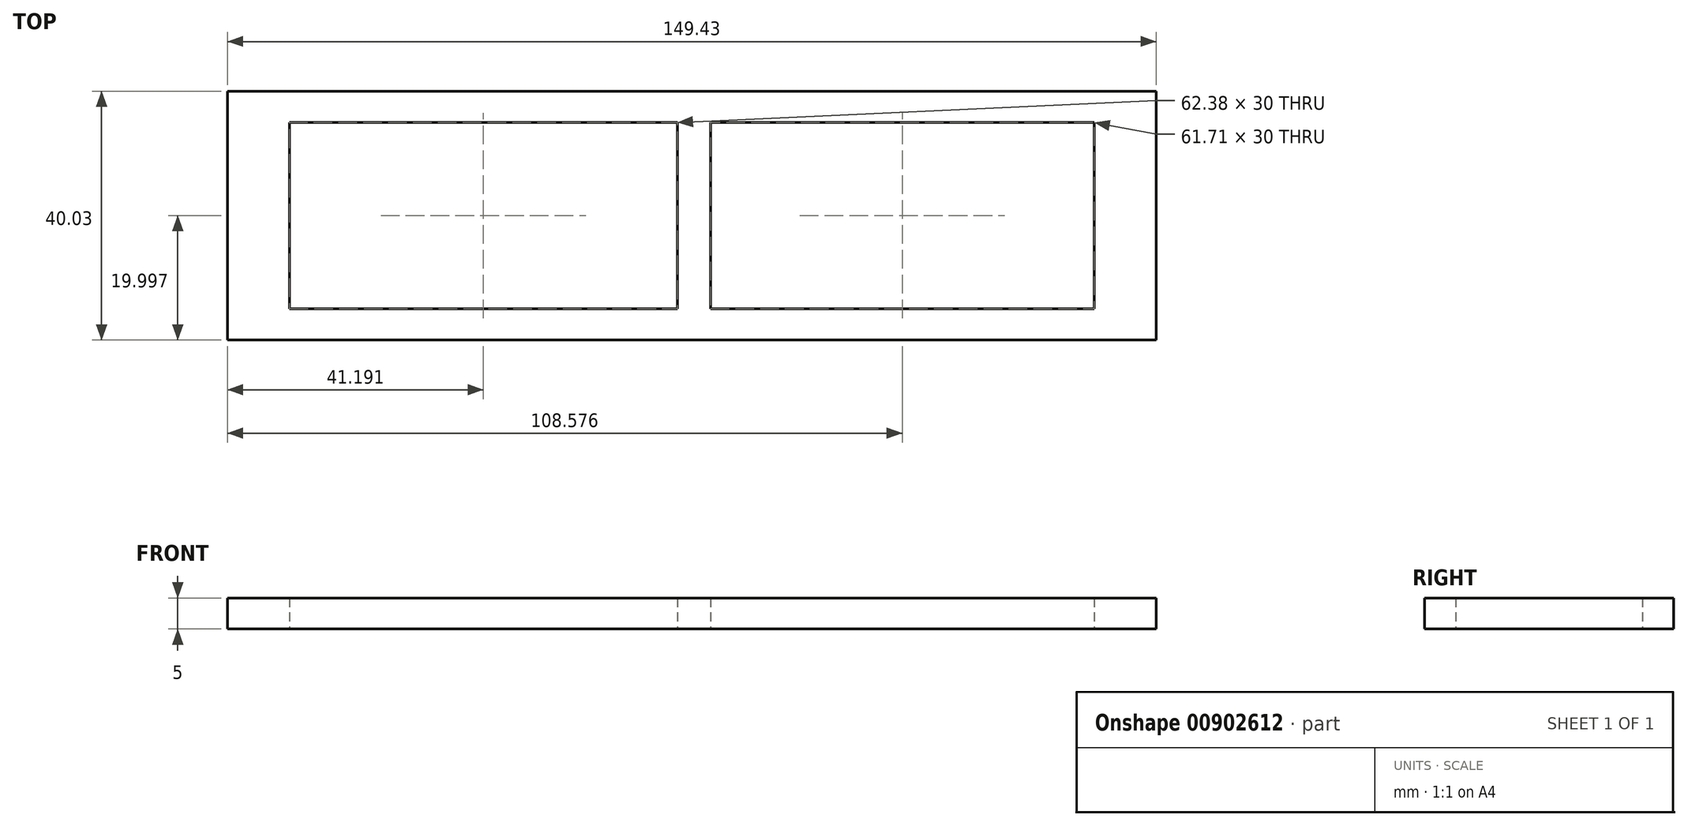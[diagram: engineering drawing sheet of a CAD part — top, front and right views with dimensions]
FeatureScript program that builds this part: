
annotation { "Feature Type Name" : "Feature", "Feature Type Description" : "" }
export const myFeature = defineFeature(function(context is Context, id is Id, definition is map)
    precondition{}
    {
        {
            var Q0;
            Q0=qCreatedBy(makeId("Top.planeOp"),FACE);
            var sketch = newSketch(context, id + "F0", { "sketchPlane" : qUnion([Q0])});
            skLineSegment(sketch, "E0.bottom", {"start": v(-75.17, 20.19) * mm, "end": v(-65.17, 20.19) * mm});
            skLineSegment(sketch, "E0.top", {"start": v(-75.17, -19.81) * mm, "end": v(-65.17, -19.81) * mm});
            skLineSegment(sketch, "E0.left", {"start": v(-75.17, 20.19) * mm, "end": v(-75.17, -19.81) * mm});
            skLineSegment(sketch, "E0.right", {"start": v(-65.17, 20.19) * mm, "end": v(-65.17, -19.81) * mm});
            skLineSegment(sketch, "E1.bottom", {"start": v(64.26, 20.22) * mm, "end": v(74.26, 20.22) * mm});
            skLineSegment(sketch, "E1.top", {"start": v(64.26, -19.78) * mm, "end": v(74.26, -19.78) * mm});
            skLineSegment(sketch, "E1.left", {"start": v(64.26, 20.22) * mm, "end": v(64.26, -19.78) * mm});
            skLineSegment(sketch, "E1.right", {"start": v(74.26, 20.22) * mm, "end": v(74.26, -19.78) * mm});
            skLineSegment(sketch, "E2.bottom", {"start": v(-75.17, 20.19) * mm, "end": v(74.26, 20.19) * mm});
            skLineSegment(sketch, "E2.top", {"start": v(-75.17, 15.19) * mm, "end": v(74.26, 15.19) * mm});
            skLineSegment(sketch, "E2.left", {"start": v(-75.17, 20.19) * mm, "end": v(-75.17, 15.19) * mm});
            skLineSegment(sketch, "E2.right", {"start": v(74.26, 20.19) * mm, "end": v(74.26, 15.19) * mm});
            skLineSegment(sketch, "E3.bottom", {"start": v(-75.17, -19.81) * mm, "end": v(74.26, -19.81) * mm});
            skLineSegment(sketch, "E3.top", {"start": v(-75.17, -14.81) * mm, "end": v(74.26, -14.81) * mm});
            skLineSegment(sketch, "E3.left", {"start": v(-75.17, -19.81) * mm, "end": v(-75.17, -14.81) * mm});
            skLineSegment(sketch, "E3.right", {"start": v(74.26, -19.81) * mm, "end": v(74.26, -14.81) * mm});
            skLineSegment(sketch, "E4.bottom", {"start": v(-2.79, 20.19) * mm, "end": v(2.55, 20.19) * mm});
            skLineSegment(sketch, "E4.top", {"start": v(-2.79, -19.81) * mm, "end": v(2.55, -19.81) * mm});
            skLineSegment(sketch, "E4.left", {"start": v(-2.79, 20.19) * mm, "end": v(-2.79, -19.81) * mm});
            skLineSegment(sketch, "E4.right", {"start": v(2.55, 20.19) * mm, "end": v(2.55, -19.81) * mm});
            skSolve(sketch);
        }
        {
            var Q0;
            Q0 = qSketchRegion(id + "F0", true);
            var Q1;
            {var subQ0=sQuery(id+"F0.wireOp",EDGE,"E4.left");var subQ1=sQuery(id+"F0.wireOp",EDGE,"E2.top");var subQ2=makeQuery(id+"F0.imprint","INTERSECT",VERTEX,{"derivedFrom":[subQ1,subQ0]});Q1=makeQuery(id+"F0.imprint","IMPRINT",FACE,{"disambiguationData":[TD([[makeQuery(id+"F0.imprint","IMPRINT",EDGE,{"disambiguationData":[TD([[subQ2,-1.0]])],"derivedFrom":subQ1}),-1.0]])]});}
            extrude(context, id + "F1", {"entities" : qUnion([Q0, Q1]), "depth" : 5 * mm, "offsetDistance" : 25 * mm});
        }
    });
